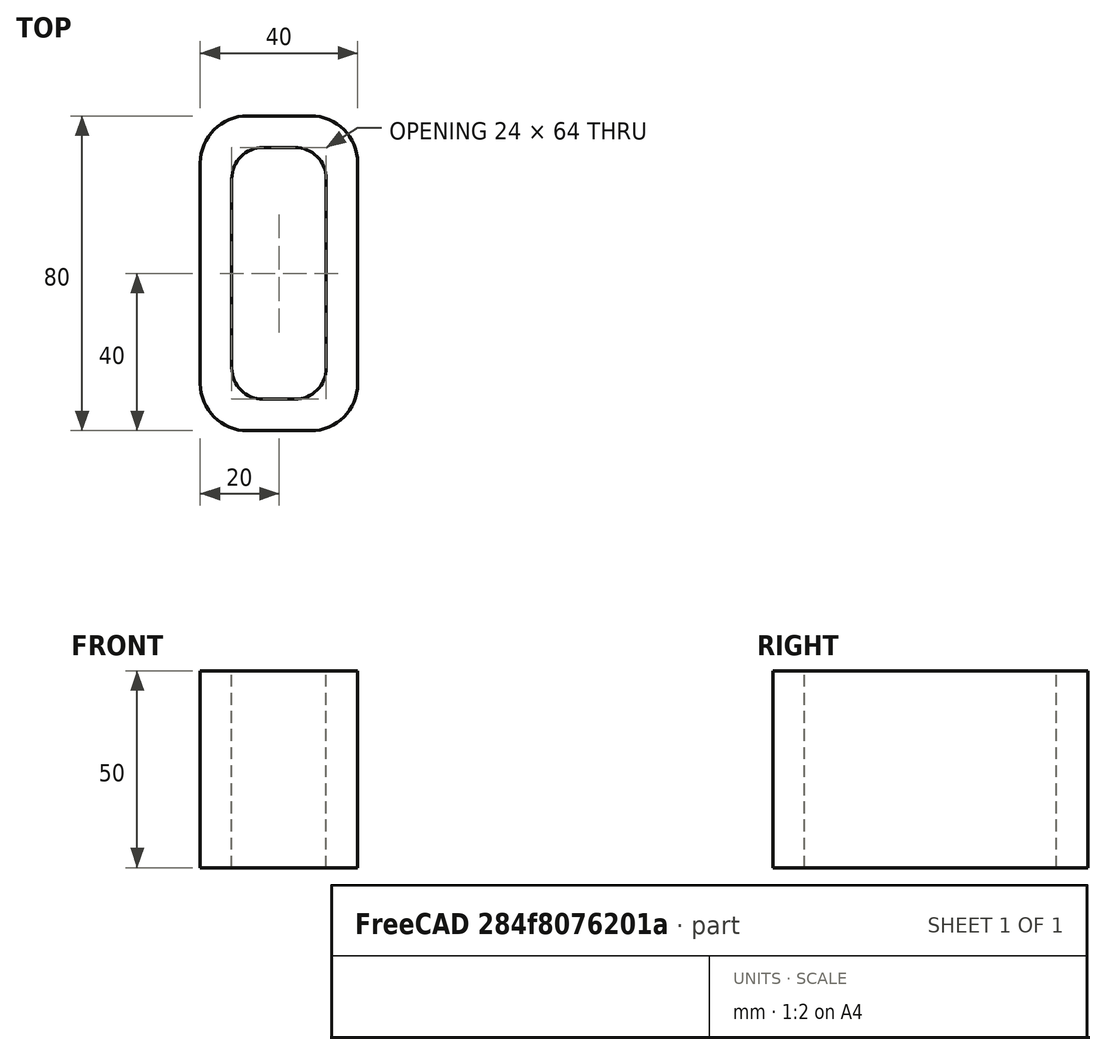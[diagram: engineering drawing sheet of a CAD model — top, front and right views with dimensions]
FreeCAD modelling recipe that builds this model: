
FCSTD DOCUMENT  (FreeCAD 0.15R4671 (Git))
Label: Rectangular hollow section 80x40x8 EN10219 S235JRH
License: All rights reserved
LicenseURL: http://en.wikipedia.org/wiki/All_rights_reserved
objects: Sketcher::SketchObject×1, Part::Extrusion×1
note: 2 computed .brp shape members not serialized (recipe doc carries the construction recipe); baked Part::Feature solids carry a one-line shape summary decoded from their .brp

FEATURE [Sketcher::SketchObject] Sketch
  sketch-geometry (16):
    g0: LineSegment StartX=-4 StartY=32 StartZ=0 EndX=4 EndY=32 EndZ=0
    g1: LineSegment StartX=12 StartY=24 StartZ=0 EndX=12 EndY=-24 EndZ=0
    g2: LineSegment StartX=4 StartY=-32 StartZ=0 EndX=-4 EndY=-32 EndZ=0
    g3: LineSegment StartX=-12 StartY=-24 StartZ=0 EndX=-12 EndY=24 EndZ=0
    g4: LineSegment StartX=-8 StartY=40 StartZ=0 EndX=8 EndY=40 EndZ=0
    g5: LineSegment StartX=20 StartY=28 StartZ=0 EndX=20 EndY=-28 EndZ=0
    g6: LineSegment StartX=8 StartY=-40 StartZ=0 EndX=-8 EndY=-40 EndZ=0
    g7: LineSegment StartX=-20 StartY=-28 StartZ=0 EndX=-20 EndY=28 EndZ=0
    g8: ArcOfCircle CenterX=-4 CenterY=24 CenterZ=0 NormalX=0 NormalY=0 NormalZ=1 Radius=8 StartAngle=1.5708 EndAngle=3.14159
    g9: ArcOfCircle CenterX=4 CenterY=24 CenterZ=0 NormalX=0 NormalY=0 NormalZ=1 Radius=8 StartAngle=-2e-12 EndAngle=1.5708
    g10: ArcOfCircle CenterX=4 CenterY=-24 CenterZ=0 NormalX=0 NormalY=0 NormalZ=1 Radius=8 StartAngle=4.71239 EndAngle=6.28319
    g11: ArcOfCircle CenterX=-4 CenterY=-24 CenterZ=0 NormalX=0 NormalY=0 NormalZ=1 Radius=8 StartAngle=3.14159 EndAngle=4.71239
    g12: ArcOfCircle CenterX=8 CenterY=28 CenterZ=0 NormalX=0 NormalY=0 NormalZ=1 Radius=12 StartAngle=0 EndAngle=1.5708
    g13: ArcOfCircle CenterX=8 CenterY=-28 CenterZ=0 NormalX=0 NormalY=0 NormalZ=1 Radius=12 StartAngle=4.71239 EndAngle=6.28319
    g14: ArcOfCircle CenterX=-8 CenterY=-28 CenterZ=0 NormalX=0 NormalY=0 NormalZ=1 Radius=12 StartAngle=3.14159 EndAngle=4.71239
    g15: ArcOfCircle CenterX=-8 CenterY=28 CenterZ=0 NormalX=0 NormalY=0 NormalZ=1 Radius=12 StartAngle=1.5708 EndAngle=3.14159
  constraints (36):
    c: Horizontal(g2)
    c: Vertical(g3)
    c: Horizontal(g6)
    c: Vertical(g7)
    c: Tangent(g3,g8) = 1.5708
    c: Tangent(g0,g8) = 1.5708
    c: Tangent(g0,g9) = 1.5708
    c: Tangent(g1,g9) = 1.5708
    c: Tangent(g1,g10) = 1.5708
    c: Tangent(g2,g10) = 1.5708
    c: Tangent(g2,g11) = 1.5708
    c: Tangent(g3,g11) = 1.5708
    c: Tangent(g4,g12) = 1.5708
    c: Tangent(g5,g12) = 1.5708
    c: Tangent(g5,g13) = 1.5708
    c: Tangent(g6,g13) = 1.5708
    c: Tangent(g6,g14) = 1.5708
    c: Tangent(g7,g14) = 1.5708
    c: Tangent(g7,g15) = 1.5708
    c: Tangent(g4,g15) = 1.5708
    c: Equal(g9,g8)
    c: Equal(g9,g11)
    c: Equal(g9,g10)
    c: Equal(g12,g15)
    c: Equal(g12,g14)
    c: Equal(g12,g13)
    c: Symmetric(g4,g6,g-1)
    c: Symmetric(g7,g5,g-2)
    c: DistanceY(g4,g6) = -80
    c: DistanceX(g7,g5) = 40
    c: Symmetric(g3,g1,g-2)
    c: Symmetric(g0,g2,g-1)
    c: DistanceY(g0,g4) = 8
    c: DistanceX(g5,g1) = -8
    c: Radius(g9) = 8
    c: Radius(g12) = 12
FEATURE [Part::Extrusion] Extrude  label="Rectangular hollow section 80x40x8 EN10219 S235JRH"
  Base = -> Sketch
  Dir = (0,0,50)
  Solid = true
